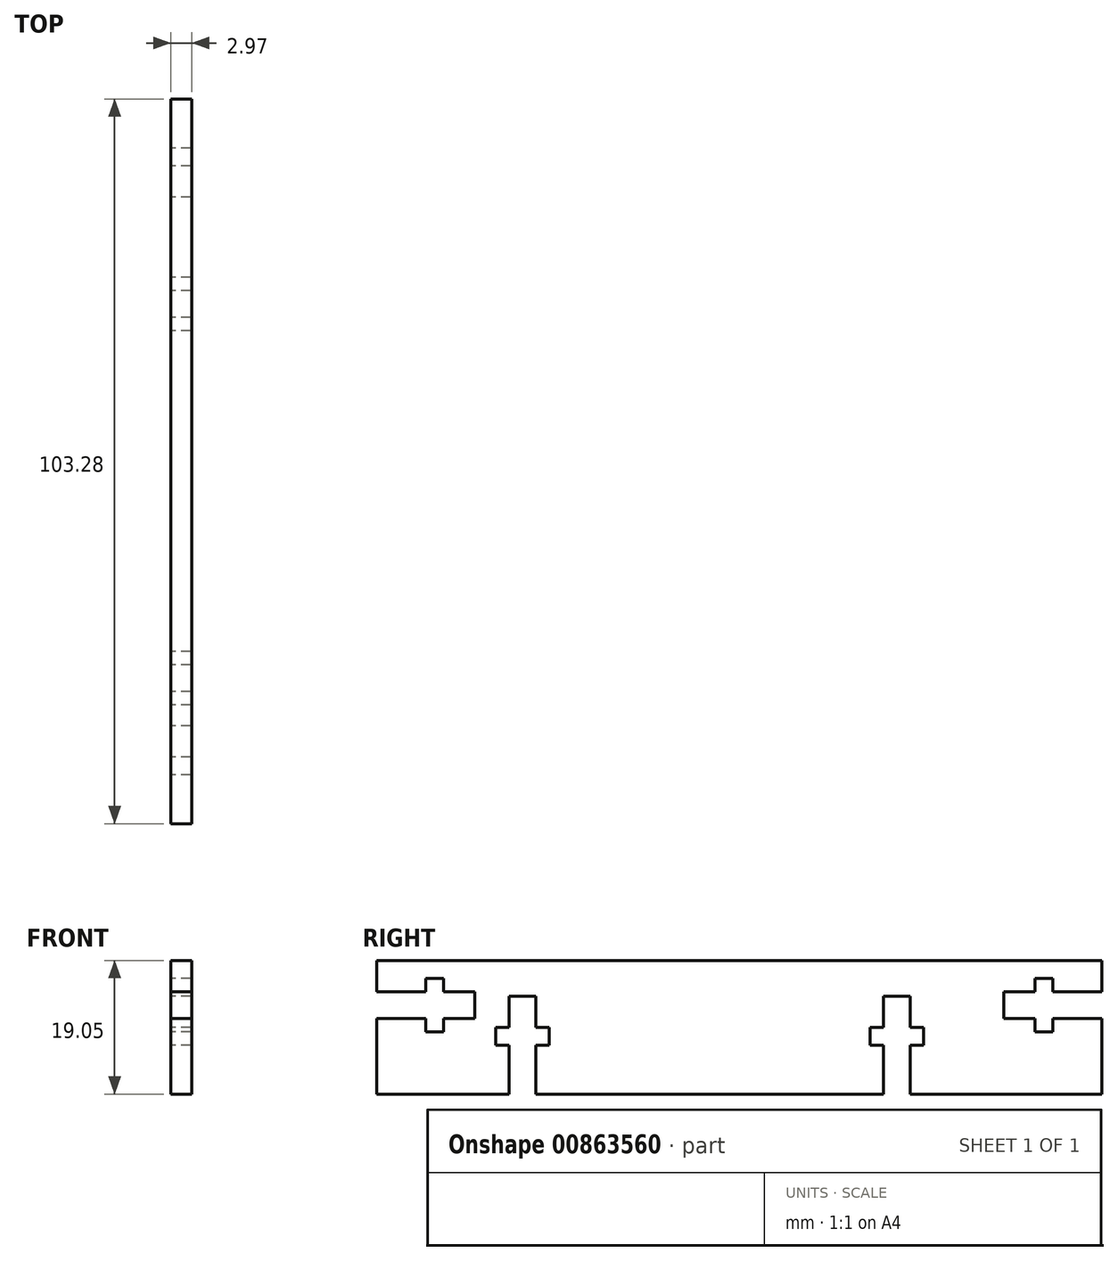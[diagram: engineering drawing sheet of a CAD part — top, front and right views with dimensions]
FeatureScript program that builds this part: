
annotation { "Feature Type Name" : "Feature", "Feature Type Description" : "" }
export const myFeature = defineFeature(function(context is Context, id is Id, definition is map)
    precondition{}
    {
        {
            var Q0;
            Q0=qCreatedBy(makeId("Right.planeOp"),FACE);
            var sketch = newSketch(context, id + "F0", { "sketchPlane" : qUnion([Q0])});
            skLineSegment(sketch, "E0.bottom", {"start": v(0, 0) * mm, "end": v(18.85, 0) * mm});
            skLineSegment(sketch, "E0.top", {"start": v(0, 19.05) * mm, "end": v(103.28, 19.05) * mm});
            skLineSegment(sketch, "E0.left", {"start": v(0, 0) * mm, "end": v(0, 10.8) * mm});
            skLineSegment(sketch, "E0.right", {"start": v(103.28, 0) * mm, "end": v(103.28, 10.8) * mm});
            skLineSegment(sketch, "E1", {"start": v(18.85, 0) * mm, "end": v(18.85, 6.98) * mm});
            skLineSegment(sketch, "E2", {"start": v(18.85, 6.98) * mm, "end": v(16.94, 6.98) * mm});
            skLineSegment(sketch, "E3", {"start": v(16.94, 6.98) * mm, "end": v(16.94, 9.52) * mm});
            skLineSegment(sketch, "E4", {"start": v(16.94, 9.52) * mm, "end": v(18.85, 9.52) * mm});
            skLineSegment(sketch, "E5", {"start": v(18.85, 9.52) * mm, "end": v(18.85, 13.97) * mm});
            skLineSegment(sketch, "E6", {"start": v(18.85, 13.97) * mm, "end": v(22.66, 13.97) * mm});
            skLineSegment(sketch, "E7", {"start": v(22.66, 13.97) * mm, "end": v(22.66, 9.53) * mm});
            skLineSegment(sketch, "E8", {"start": v(22.66, 9.53) * mm, "end": v(24.56, 9.53) * mm});
            skLineSegment(sketch, "E9", {"start": v(24.56, 9.53) * mm, "end": v(24.56, 6.98) * mm});
            skLineSegment(sketch, "E10", {"start": v(24.56, 6.98) * mm, "end": v(22.66, 6.98) * mm});
            skLineSegment(sketch, "E11", {"start": v(22.66, 6.98) * mm, "end": v(22.66, 0) * mm});
            skLineSegment(sketch, "E12", {"start": v(0, 14.6) * mm, "end": v(6.99, 14.6) * mm});
            skLineSegment(sketch, "E13", {"start": v(6.99, 14.6) * mm, "end": v(6.99, 16.5) * mm});
            skLineSegment(sketch, "E14", {"start": v(6.99, 16.51) * mm, "end": v(9.53, 16.51) * mm});
            skLineSegment(sketch, "E15", {"start": v(9.53, 16.5) * mm, "end": v(9.53, 14.6) * mm});
            skLineSegment(sketch, "E16", {"start": v(9.53, 14.6) * mm, "end": v(13.97, 14.6) * mm});
            skLineSegment(sketch, "E17", {"start": v(13.97, 14.6) * mm, "end": v(13.97, 10.8) * mm});
            skLineSegment(sketch, "E18", {"start": v(13.97, 10.8) * mm, "end": v(9.53, 10.8) * mm});
            skLineSegment(sketch, "E19", {"start": v(9.53, 10.8) * mm, "end": v(9.53, 8.89) * mm});
            skLineSegment(sketch, "E20", {"start": v(9.53, 8.9) * mm, "end": v(6.98, 8.9) * mm});
            skLineSegment(sketch, "E21", {"start": v(6.99, 8.89) * mm, "end": v(6.99, 10.8) * mm});
            skLineSegment(sketch, "E22", {"start": v(6.98, 10.8) * mm, "end": v(0, 10.8) * mm});
            skLineSegment(sketch, "E23", {"start": v(72.19, 0) * mm, "end": v(72.19, 6.98) * mm});
            skLineSegment(sketch, "E24", {"start": v(72.19, 6.98) * mm, "end": v(70.28, 6.98) * mm});
            skLineSegment(sketch, "E25", {"start": v(70.28, 6.98) * mm, "end": v(70.28, 9.52) * mm});
            skLineSegment(sketch, "E26", {"start": v(70.28, 9.52) * mm, "end": v(72.19, 9.52) * mm});
            skLineSegment(sketch, "E27", {"start": v(72.19, 9.52) * mm, "end": v(72.19, 13.97) * mm});
            skLineSegment(sketch, "E28", {"start": v(72.19, 13.97) * mm, "end": v(76, 13.97) * mm});
            skLineSegment(sketch, "E29", {"start": v(76, 13.97) * mm, "end": v(76, 9.52) * mm});
            skLineSegment(sketch, "E30", {"start": v(76, 9.53) * mm, "end": v(77.9, 9.53) * mm});
            skLineSegment(sketch, "E31", {"start": v(77.9, 9.52) * mm, "end": v(77.9, 6.98) * mm});
            skLineSegment(sketch, "E32", {"start": v(77.9, 6.99) * mm, "end": v(76, 6.99) * mm});
            skLineSegment(sketch, "E33", {"start": v(76, 6.98) * mm, "end": v(76, 0) * mm});
            skLineSegment(sketch, "E34.trimOffspring", {"start": v(22.66, 0) * mm, "end": v(72.19, 0) * mm});
            skLineSegment(sketch, "E35.trimOffspring", {"start": v(76, 0) * mm, "end": v(103.28, 0) * mm});
            skLineSegment(sketch, "E36.trimOffspring", {"start": v(0, 14.6) * mm, "end": v(0, 19.05) * mm});
            skLineSegment(sketch, "E37", {"start": v(47.42, 0) * mm, "end": v(47.42, 19.05) * mm, "construction": true});
            skLineSegment(sketch, "E38", {"start": v(103.28, 10.8) * mm, "end": v(96.3, 10.8) * mm});
            skLineSegment(sketch, "E39", {"start": v(96.3, 10.8) * mm, "end": v(96.3, 8.9) * mm});
            skLineSegment(sketch, "E40", {"start": v(96.3, 8.9) * mm, "end": v(93.75, 8.9) * mm});
            skLineSegment(sketch, "E41", {"start": v(93.75, 8.9) * mm, "end": v(93.75, 10.8) * mm});
            skLineSegment(sketch, "E42", {"start": v(93.75, 10.8) * mm, "end": v(89.3, 10.8) * mm});
            skLineSegment(sketch, "E43", {"start": v(89.3, 10.8) * mm, "end": v(89.3, 14.6) * mm});
            skLineSegment(sketch, "E44", {"start": v(89.3, 14.6) * mm, "end": v(93.75, 14.6) * mm});
            skLineSegment(sketch, "E45", {"start": v(93.75, 14.6) * mm, "end": v(93.75, 16.51) * mm});
            skLineSegment(sketch, "E46", {"start": v(93.75, 16.51) * mm, "end": v(96.3, 16.51) * mm});
            skLineSegment(sketch, "E47", {"start": v(96.3, 16.5) * mm, "end": v(96.3, 14.6) * mm});
            skLineSegment(sketch, "E48", {"start": v(96.3, 14.6) * mm, "end": v(103.28, 14.6) * mm});
            skLineSegment(sketch, "E49.trimOffspring", {"start": v(103.28, 14.6) * mm, "end": v(103.28, 19.05) * mm});
            skSolve(sketch);
        }
        {
            var Q0;
            Q0=makeQuery(id+"F0.imprint","IMPRINT",FACE,{"disambiguationData":[TD([[makeQuery(id+"F0.imprint","IMPRINT",EDGE,{"derivedFrom":sQuery(id+"F0.wireOp",EDGE,"E0.bottom")}),1.0]])]});
            extrude(context, id + "F1", {"entities" : qUnion([Q0]), "depth" : 2.97 * mm, "offsetDistance" : 25.4 * mm});
        }
    });
